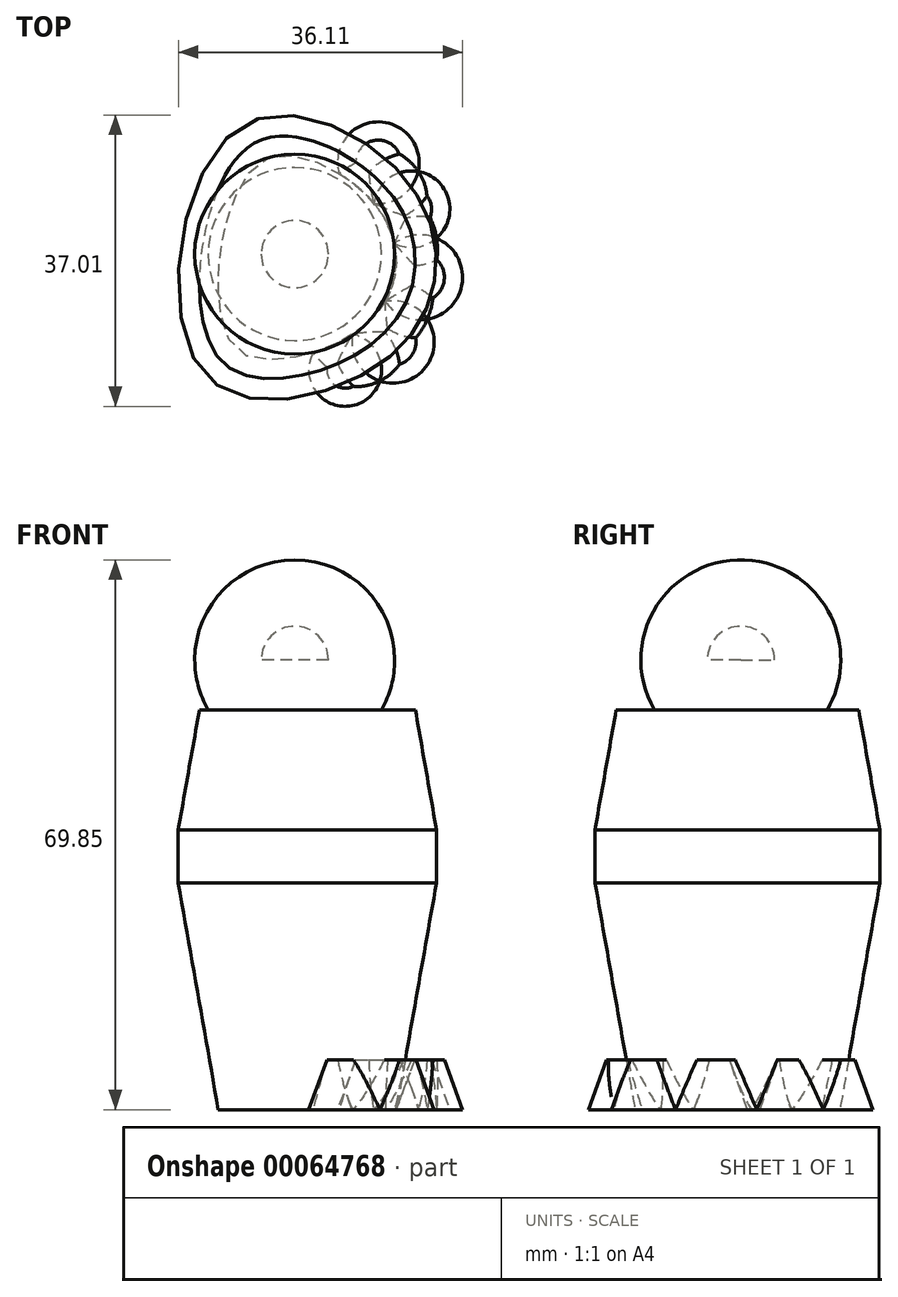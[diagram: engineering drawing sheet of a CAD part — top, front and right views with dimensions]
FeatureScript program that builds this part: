
annotation { "Feature Type Name" : "Feature", "Feature Type Description" : "" }
export const myFeature = defineFeature(function(context is Context, id is Id, definition is map)
    precondition{}
    {
        {
            var Q0;
            Q0=qCreatedBy(makeId("Top.planeOp"),FACE);
            var sketch = newSketch(context, id + "F0", { "sketchPlane" : qUnion([Q0])});
            skFitSpline(sketch, "E0", {"points": [v(-56.93, 37.15) * mm, v(-51.97, 22.74) * mm, v(-61.35, 10.73) * mm, v(-81.65, 11.48) * mm, v(-77.25, 41.96) * mm, v(-56.93, 37.15) * mm]});
            skSolve(sketch);
        }
        {
            var Q0;
            Q0=makeQuery(id+"F0.imprint","IMPRINT",FACE,{"disambiguationData":[TD([[makeQuery(id+"F0.imprint","IMPRINT",EDGE,{"derivedFrom":sQuery(id+"F0.wireOp",EDGE,"E0")}),-1.0]])]});
            extrude(context, id + "F1", {"entities" : qUnion([Q0]), "depth" : 50.8 * mm});
        }
        {
            var Q0;
            Q0=makeQuery(id+"F1.opExtrude","CAP_EDGE",EDGE,{"disambiguationData":[OSD([sQuery(id+"F0.wireOp",EDGE,"E0")])],"isStart":true});
            chamfer(context, id + "F2", {"entities" : qUnion([Q0]), "chamferType" : ChamferType.OFFSET_ANGLE, "width" : 5.08 * mm, "oppositeDirection" : false, "angle" : 80 * degree, "tangentPropagation" : true});
        }
        {
            var Q0;
            Q0=makeQuery(id+"F1.opExtrude","CAP_EDGE",EDGE,{"disambiguationData":[OSD([sQuery(id+"F0.wireOp",EDGE,"E0")])],"isStart":false});
            chamfer(context, id + "F3", {"entities" : qUnion([Q0]), "chamferType" : ChamferType.OFFSET_ANGLE, "width" : 15.24 * mm, "oppositeDirection" : false, "angle" : 10 * degree, "tangentPropagation" : true});
        }
        {
            var Q0;
            Q0=makeQuery(id+"F1.opExtrude","CAP_FACE",FACE,{"disambiguationData":[OSD([sQuery(id+"F0.wireOp",EDGE,"E0")])],"isStart":false});
            var sketch = newSketch(context, id + "F4", { "sketchPlane" : qUnion([Q0])});
            skCircle(sketch, "E1", {"center": v(-69.75, 26.2) * mm, "radius": 4.27 * mm});
            skSolve(sketch);
        }
        {
            var Q0;
            Q0 = qSketchRegion(id + "F4", true);
            extrude(context, id + "F5", {"entities" : qUnion([Q0]), "operationType" : NewBodyOperationType.ADD, "depth" : 6.35 * mm});
        }
        {
            var Q0;
            Q0=makeQuery(id+"F5.opExtrude","CAP_FACE",FACE,{"disambiguationData":[OSD([sQuery(id+"F4.wireOp",EDGE,"E1")])],"isStart":false});
            var sketch = newSketch(context, id + "F6", { "sketchPlane" : qUnion([Q0])});
            skArc(sketch, "E2", {"start": v(-57.05, 26.2) * mm, "mid": v(-69.75, 38.9) * mm, "end": v(-82.45, 26.2) * mm});
            skLineSegment(sketch, "E3", {"start": v(-82.45, 26.2) * mm, "end": v(-57.05, 26.2) * mm});
            skSolve(sketch);
        }
        {
            var Q0;
            {var subQ0=sQuery(id+"F6.wireOp",EDGE,"E2");Q0=makeQuery(id+"F6.imprint","IMPRINT",FACE,{"disambiguationData":[TD([[makeQuery(id+"F6.imprint","IMPRINT",EDGE,{"derivedFrom":subQ0}),1.0]])]});}
            var Q1;
            Q1=sQuery(id+"F6.wireOp",EDGE,"E3");
            revolve(context, id + "F7", {"operationType" : NewBodyOperationType.ADD, "entities" : qUnion([Q0]), "axis" : qUnion([Q1]), "revolveType" : RevolveType.FULL});
        }
        {
            var Q0;
            Q0=makeQuery(id+"F1.opExtrude","CAP_FACE",FACE,{"disambiguationData":[OSD([sQuery(id+"F0.wireOp",EDGE,"E0")])],"isStart":true});
            var sketch = newSketch(context, id + "F8", { "sketchPlane" : qUnion([Q0])});
            skArc(sketch, "E4", {"start": v(-62.39, -16) * mm, "mid": v(-61.4, -7.29) * mm, "end": v(-67.43, -13.66) * mm});
            skArc(sketch, "E5", {"start": v(-58.26, -20.15) * mm, "mid": v(-53.55, -11.34) * mm, "end": v(-62.39, -16) * mm});
            skArc(sketch, "E6", {"start": v(-57.07, -27.57) * mm, "mid": v(-48.5, -22.39) * mm, "end": v(-58.26, -20.15) * mm});
            skArc(sketch, "E7", {"start": v(-59.7, -32.66) * mm, "mid": v(-50.58, -34.13) * mm, "end": v(-57.07, -27.57) * mm});
            skArc(sketch, "E8", {"start": v(-64.12, -36.42) * mm, "mid": v(-55.78, -41.77) * mm, "end": v(-59.7, -32.66) * mm});
            skSolve(sketch);
        }
        {
            var Q0;
            {var subQ0=sQuery(id+"F8.wireOp",EDGE,"E4");var subQ4=sQuery(id+"F8.wireOp",EDGE,"E5");var subQ5=makeQuery(id+"F8.imprint","INTERSECT",VERTEX,{"derivedFrom":[subQ0,subQ4]});Q0=makeQuery(id+"F8.imprint","IMPRINT",FACE,{"disambiguationData":[TD([[makeQuery(id+"F8.imprint","IMPRINT",EDGE,{"disambiguationData":[TD([[subQ5,-1.0]])],"derivedFrom":subQ0}),1.0]])]});}
            var Q1;
            {var subQ0=sQuery(id+"F8.wireOp",EDGE,"E5");var subQ1=sQuery(id+"F8.wireOp",EDGE,"E4");var subQ5=makeQuery(id+"F8.imprint","INTERSECT",VERTEX,{"derivedFrom":[subQ1,subQ0]});Q1=makeQuery(id+"F8.imprint","IMPRINT",FACE,{"disambiguationData":[TD([[makeQuery(id+"F8.imprint","IMPRINT",EDGE,{"disambiguationData":[TD([[subQ5,1.0]])],"derivedFrom":subQ0}),1.0]])]});}
            var Q2;
            {var subQ0=sQuery(id+"F8.wireOp",EDGE,"E6");var subQ1=sQuery(id+"F8.wireOp",EDGE,"E5");var subQ5=makeQuery(id+"F8.imprint","INTERSECT",VERTEX,{"derivedFrom":[subQ1,subQ0]});Q2=makeQuery(id+"F8.imprint","IMPRINT",FACE,{"disambiguationData":[TD([[makeQuery(id+"F8.imprint","IMPRINT",EDGE,{"disambiguationData":[TD([[subQ5,1.0]])],"derivedFrom":subQ0}),1.0]])]});}
            var Q3;
            {var subQ0=sQuery(id+"F8.wireOp",EDGE,"E7");var subQ1=sQuery(id+"F8.wireOp",EDGE,"E6");var subQ5=makeQuery(id+"F8.imprint","INTERSECT",VERTEX,{"derivedFrom":[subQ1,subQ0]});Q3=makeQuery(id+"F8.imprint","IMPRINT",FACE,{"disambiguationData":[TD([[makeQuery(id+"F8.imprint","IMPRINT",EDGE,{"disambiguationData":[TD([[subQ5,1.0]])],"derivedFrom":subQ0}),1.0]])]});}
            var Q4;
            {var subQ0=sQuery(id+"F8.wireOp",EDGE,"E8");var subQ1=sQuery(id+"F8.wireOp",EDGE,"E7");var subQ5=makeQuery(id+"F8.imprint","INTERSECT",VERTEX,{"derivedFrom":[subQ1,subQ0]});Q4=makeQuery(id+"F8.imprint","IMPRINT",FACE,{"disambiguationData":[TD([[makeQuery(id+"F8.imprint","IMPRINT",EDGE,{"disambiguationData":[TD([[subQ5,1.0]])],"derivedFrom":subQ0}),1.0]])]});}
            extrude(context, id + "F9", {"entities" : qUnion([Q0, Q1, Q2, Q3, Q4]), "operationType" : NewBodyOperationType.ADD, "oppositeDirection" : true, "depth" : 6.35 * mm, "hasDraft" : true, "draftAngle" : 20 * degree, "draftPullDirection" : true});
        }
    });
